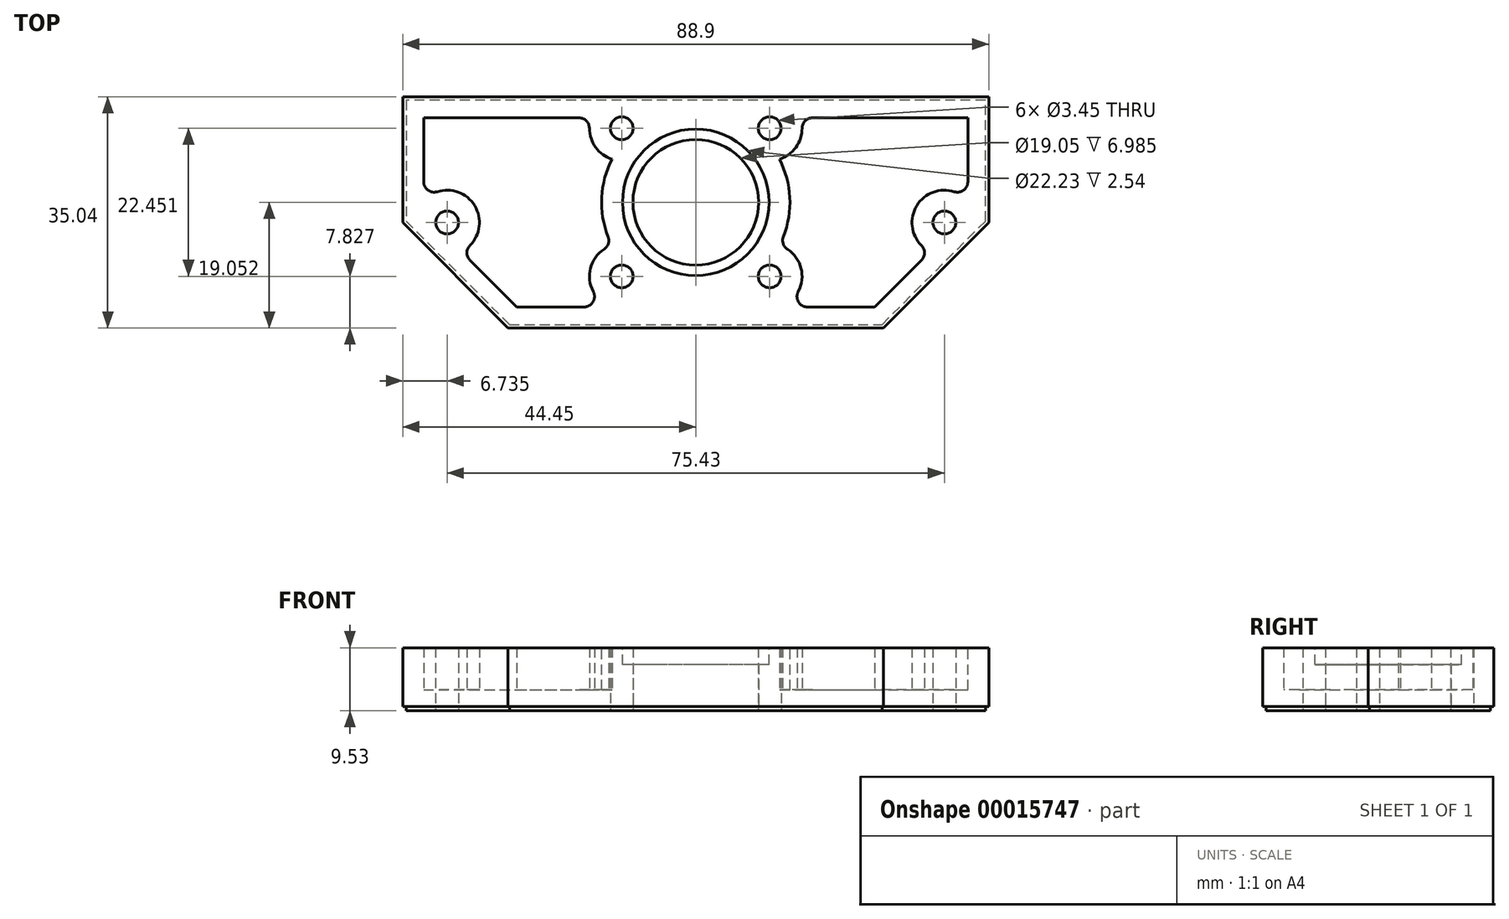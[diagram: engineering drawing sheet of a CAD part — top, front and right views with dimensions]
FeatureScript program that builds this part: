
annotation { "Feature Type Name" : "Feature", "Feature Type Description" : "" }
export const myFeature = defineFeature(function(context is Context, id is Id, definition is map)
    precondition{}
    {
        {
            var Q0;
            Q0=qCreatedBy(makeId("Top.planeOp"),FACE);
            var sketch = newSketch(context, id + "F0", { "sketchPlane" : qUnion([Q0])});
            skLineSegment(sketch, "E0.bottom", {"start": v(0, 0) * mm, "end": v(88.9, 0) * mm});
            skLineSegment(sketch, "E0.left", {"start": v(0, 0) * mm, "end": v(0, -19.05) * mm});
            skLineSegment(sketch, "E0.right", {"start": v(88.9, 0) * mm, "end": v(88.9, -19.05) * mm});
            skLineSegment(sketch, "E1", {"start": v(0, -19.05) * mm, "end": v(15.99, -35.04) * mm});
            skLineSegment(sketch, "E2", {"start": v(88.9, -19.05) * mm, "end": v(72.91, -35.04) * mm});
            skLineSegment(sketch, "E3", {"start": v(15.99, -35.04) * mm, "end": v(72.91, -35.04) * mm});
            skLineSegment(sketch, "E4", {"start": v(0, -19.05) * mm, "end": v(6.74, -19.05) * mm, "construction": true});
            skCircle(sketch, "E5", {"center": v(6.74, -19.05) * mm, "radius": 4.76 * mm, "construction": true});
            skLineSegment(sketch, "E6", {"start": v(88.9, -19.05) * mm, "end": v(82.16, -19.05) * mm, "construction": true});
            skLineSegment(sketch, "E7", {"start": v(44.45, -15.99) * mm, "end": v(44.45, -35.04) * mm, "construction": true});
            skCircle(sketch, "E8", {"center": v(44.45, -15.99) * mm, "radius": 9.53 * mm});
            skCircle(sketch, "E9", {"center": v(6.74, -19.05) * mm, "radius": 1.73 * mm});
            skCircle(sketch, "E10", {"center": v(82.16, -19.05) * mm, "radius": 1.73 * mm});
            skLineSegment(sketch, "E11.bottom", {"start": v(55.68, -27.21) * mm, "end": v(33.22, -27.21) * mm, "construction": true});
            skLineSegment(sketch, "E11.top", {"start": v(55.68, -4.76) * mm, "end": v(33.22, -4.76) * mm, "construction": true});
            skLineSegment(sketch, "E11.left", {"start": v(55.68, -27.21) * mm, "end": v(55.68, -4.76) * mm, "construction": true});
            skLineSegment(sketch, "E11.right", {"start": v(33.22, -27.21) * mm, "end": v(33.22, -4.76) * mm, "construction": true});
            skCircle(sketch, "E12", {"center": v(44.45, -15.99) * mm, "radius": 11.11 * mm, "construction": true});
            skCircle(sketch, "E13", {"center": v(55.68, -4.76) * mm, "radius": 4.76 * mm, "construction": true});
            skCircle(sketch, "E14", {"center": v(33.22, -4.76) * mm, "radius": 1.73 * mm});
            skCircle(sketch, "E15", {"center": v(55.68, -4.76) * mm, "radius": 1.73 * mm});
            skCircle(sketch, "E16", {"center": v(55.68, -27.21) * mm, "radius": 1.73 * mm});
            skCircle(sketch, "E17", {"center": v(33.22, -27.21) * mm, "radius": 1.73 * mm});
            skLineSegment(sketch, "E18", {"start": v(6.74, -19.05) * mm, "end": v(15.99, -19.05) * mm, "construction": true});
            skLineSegment(sketch, "E19", {"start": v(15.99, -19.05) * mm, "end": v(15.99, -35.04) * mm, "construction": true});
            skSolve(sketch);
        }
        {
            var Q0;
            Q0=qSketchRegion(id+"F0",true);
            extrude(context, id + "F1", {"entities" : qUnion([Q0]), "depth" : 9.52 * mm});
        }
        {
            var Q0;
            Q0=makeQuery(id+"F1.opExtrude","CAP_FACE",FACE,{"disambiguationData":[OSD([sQuery(id+"F0.wireOp",EDGE,"E0.bottom"),sQuery(id+"F0.wireOp",EDGE,"E0.left"),sQuery(id+"F0.wireOp",EDGE,"E0.right"),sQuery(id+"F0.wireOp",EDGE,"E1"),sQuery(id+"F0.wireOp",EDGE,"E2"),sQuery(id+"F0.wireOp",EDGE,"E3"),sQuery(id+"F0.wireOp",EDGE,"E8"),sQuery(id+"F0.wireOp",EDGE,"E9"),sQuery(id+"F0.wireOp",EDGE,"E10"),sQuery(id+"F0.wireOp",EDGE,"E14"),sQuery(id+"F0.wireOp",EDGE,"E15"),sQuery(id+"F0.wireOp",EDGE,"E16"),sQuery(id+"F0.wireOp",EDGE,"E17")])],"isStart":false});
            var sketch = newSketch(context, id + "F2", { "sketchPlane" : qUnion([Q0])});
            skCircle(sketch, "E20", {"center": v(44.45, -15.99) * mm, "radius": 11.11 * mm});
            skSolve(sketch);
        }
        {
            var Q0;
            Q0=qSketchRegion(id+"F2",true);
            extrude(context, id + "F3", {"entities" : qUnion([Q0]), "operationType" : NewBodyOperationType.REMOVE, "oppositeDirection" : true, "depth" : 2.54 * mm});
        }
        {
            var Q0;
            Q0=makeQuery(id+"F1.opExtrude","CAP_FACE",FACE,{"disambiguationData":[OSD([sQuery(id+"F0.wireOp",EDGE,"E0.bottom"),sQuery(id+"F0.wireOp",EDGE,"E0.left"),sQuery(id+"F0.wireOp",EDGE,"E0.right"),sQuery(id+"F0.wireOp",EDGE,"E1"),sQuery(id+"F0.wireOp",EDGE,"E2"),sQuery(id+"F0.wireOp",EDGE,"E3"),sQuery(id+"F0.wireOp",EDGE,"E8"),sQuery(id+"F0.wireOp",EDGE,"E9"),sQuery(id+"F0.wireOp",EDGE,"E10"),sQuery(id+"F0.wireOp",EDGE,"E14"),sQuery(id+"F0.wireOp",EDGE,"E15"),sQuery(id+"F0.wireOp",EDGE,"E16"),sQuery(id+"F0.wireOp",EDGE,"E17")])],"isStart":false});
            shell(context, id + "F4", {"entities" : qUnion([Q0]), "thickness" : 3.17 * mm});
        }
        {
            var Q0;
            Q0=makeQuery(id+"F4.opShell","OFFSET_FACE",FACE,{"disambiguationData":[OSD([sQuery(id+"F0.wireOp",EDGE,"E0.bottom"),sQuery(id+"F0.wireOp",EDGE,"E0.left"),sQuery(id+"F0.wireOp",EDGE,"E0.right"),sQuery(id+"F0.wireOp",EDGE,"E1"),sQuery(id+"F0.wireOp",EDGE,"E2"),sQuery(id+"F0.wireOp",EDGE,"E3"),sQuery(id+"F0.wireOp",EDGE,"E8"),sQuery(id+"F0.wireOp",EDGE,"E9"),sQuery(id+"F0.wireOp",EDGE,"E10"),sQuery(id+"F0.wireOp",EDGE,"E14"),sQuery(id+"F0.wireOp",EDGE,"E15"),sQuery(id+"F0.wireOp",EDGE,"E16"),sQuery(id+"F0.wireOp",EDGE,"E17")]),OD(2.0)]});
            var Q1;
            Q1=makeQuery(id+"F4.opShell","OFFSET_FACE",FACE,{"disambiguationData":[OSD([sQuery(id+"F0.wireOp",EDGE,"E0.bottom"),sQuery(id+"F0.wireOp",EDGE,"E0.left"),sQuery(id+"F0.wireOp",EDGE,"E0.right"),sQuery(id+"F0.wireOp",EDGE,"E1"),sQuery(id+"F0.wireOp",EDGE,"E2"),sQuery(id+"F0.wireOp",EDGE,"E3"),sQuery(id+"F0.wireOp",EDGE,"E8"),sQuery(id+"F0.wireOp",EDGE,"E9"),sQuery(id+"F0.wireOp",EDGE,"E10"),sQuery(id+"F0.wireOp",EDGE,"E14"),sQuery(id+"F0.wireOp",EDGE,"E15"),sQuery(id+"F0.wireOp",EDGE,"E16"),sQuery(id+"F0.wireOp",EDGE,"E17")]),OD(3.0)]});
            var Q2;
            Q2=makeQuery(id+"F1.opExtrude","CAP_FACE",FACE,{"disambiguationData":[OSD([sQuery(id+"F0.wireOp",EDGE,"E0.bottom"),sQuery(id+"F0.wireOp",EDGE,"E0.left"),sQuery(id+"F0.wireOp",EDGE,"E0.right"),sQuery(id+"F0.wireOp",EDGE,"E1"),sQuery(id+"F0.wireOp",EDGE,"E2"),sQuery(id+"F0.wireOp",EDGE,"E3"),sQuery(id+"F0.wireOp",EDGE,"E8"),sQuery(id+"F0.wireOp",EDGE,"E9"),sQuery(id+"F0.wireOp",EDGE,"E10"),sQuery(id+"F0.wireOp",EDGE,"E14"),sQuery(id+"F0.wireOp",EDGE,"E15"),sQuery(id+"F0.wireOp",EDGE,"E16"),sQuery(id+"F0.wireOp",EDGE,"E17")])],"isStart":false});
            extrude(context, id + "F5", {"entities" : qUnion([Q0, Q1]), "operationType" : NewBodyOperationType.ADD, "endBound" : BoundingType.UP_TO_SURFACE, "endBoundEntityFace" : qUnion([Q2]), "depth" : 25.4 * mm});
        }
        {
            var Q0;
            Q0=makeQuery(id+"F4.opShell","TWEAK_EDGE",EDGE,{"derivedFrom":[makeQuery(id+"F1.opExtrude","SWEPT_FACE",FACE,{"disambiguationData":[OSD([sQuery(id+"F0.wireOp",EDGE,"E0.left")])]}),makeQuery(id+"F1.opExtrude","SWEPT_FACE",FACE,{"disambiguationData":[OSD([sQuery(id+"F0.wireOp",EDGE,"E9")])]})]});
            var Q1;
            Q1=makeQuery(id+"F4.opShell","TWEAK_EDGE",EDGE,{"derivedFrom":[makeQuery(id+"F1.opExtrude","SWEPT_FACE",FACE,{"disambiguationData":[OSD([sQuery(id+"F0.wireOp",EDGE,"E1")])]}),makeQuery(id+"F1.opExtrude","SWEPT_FACE",FACE,{"disambiguationData":[OSD([sQuery(id+"F0.wireOp",EDGE,"E9")])]})]});
            var Q2;
            Q2=makeQuery(id+"F4.opShell","TWEAK_EDGE",EDGE,{"disambiguationData":[OD(0.0)],"derivedFrom":[makeQuery(id+"F1.opExtrude","SWEPT_FACE",FACE,{"disambiguationData":[OSD([sQuery(id+"F0.wireOp",EDGE,"E3")])]}),makeQuery(id+"F1.opExtrude","SWEPT_FACE",FACE,{"disambiguationData":[OSD([sQuery(id+"F0.wireOp",EDGE,"E17")])]})]});
            var Q3;
            Q3=makeQuery(id+"F4.opShell","TWEAK_EDGE",EDGE,{"disambiguationData":[OD(0.0)],"derivedFrom":[makeQuery(id+"F1.opExtrude","SWEPT_FACE",FACE,{"disambiguationData":[OSD([sQuery(id+"F0.wireOp",EDGE,"E0.bottom")])]}),makeQuery(id+"F1.opExtrude","SWEPT_FACE",FACE,{"disambiguationData":[OSD([sQuery(id+"F0.wireOp",EDGE,"E14")])]})]});
            var Q4;
            Q4=makeQuery(id+"F4.opShell","TWEAK_EDGE",EDGE,{"disambiguationData":[OD(0.0)],"derivedFrom":[makeQuery(id+"F1.opExtrude","SWEPT_FACE",FACE,{"disambiguationData":[OSD([sQuery(id+"F0.wireOp",EDGE,"E0.bottom")])]}),makeQuery(id+"F1.opExtrude","SWEPT_FACE",FACE,{"disambiguationData":[OSD([sQuery(id+"F0.wireOp",EDGE,"E15")])]})]});
            var Q5;
            Q5=makeQuery(id+"F4.opShell","TWEAK_EDGE",EDGE,{"disambiguationData":[OD(0.0)],"derivedFrom":[makeQuery(id+"F1.opExtrude","SWEPT_FACE",FACE,{"disambiguationData":[OSD([sQuery(id+"F0.wireOp",EDGE,"E3")])]}),makeQuery(id+"F1.opExtrude","SWEPT_FACE",FACE,{"disambiguationData":[OSD([sQuery(id+"F0.wireOp",EDGE,"E16")])]})]});
            var Q6;
            Q6=makeQuery(id+"F4.opShell","TWEAK_EDGE",EDGE,{"derivedFrom":[makeQuery(id+"F1.opExtrude","SWEPT_FACE",FACE,{"disambiguationData":[OSD([sQuery(id+"F0.wireOp",EDGE,"E2")])]}),makeQuery(id+"F1.opExtrude","SWEPT_FACE",FACE,{"disambiguationData":[OSD([sQuery(id+"F0.wireOp",EDGE,"E10")])]})]});
            var Q7;
            Q7=makeQuery(id+"F4.opShell","TWEAK_EDGE",EDGE,{"derivedFrom":[makeQuery(id+"F1.opExtrude","SWEPT_FACE",FACE,{"disambiguationData":[OSD([sQuery(id+"F0.wireOp",EDGE,"E0.right")])]}),makeQuery(id+"F1.opExtrude","SWEPT_FACE",FACE,{"disambiguationData":[OSD([sQuery(id+"F0.wireOp",EDGE,"E10")])]})]});
            var Q8;
            Q8=makeQuery(id+"F4.opShell","TWEAK_EDGE",EDGE,{"disambiguationData":[OD(0.0)],"derivedFrom":[makeQuery(id+"F1.opExtrude","SWEPT_FACE",FACE,{"disambiguationData":[OSD([sQuery(id+"F0.wireOp",EDGE,"E17")])]}),makeQuery(id+"F3.boolean.opBoolean","COPY",FACE,{"derivedFrom":makeQuery(id+"F3.opExtrude","SWEPT_FACE",FACE,{"disambiguationData":[OSD([sQuery(id+"F2.wireOp",EDGE,"E20")])]})})]});
            var Q9;
            Q9=makeQuery(id+"F4.opShell","TWEAK_EDGE",EDGE,{"disambiguationData":[OD(0.0)],"derivedFrom":[makeQuery(id+"F1.opExtrude","SWEPT_FACE",FACE,{"disambiguationData":[OSD([sQuery(id+"F0.wireOp",EDGE,"E16")])]}),makeQuery(id+"F3.boolean.opBoolean","COPY",FACE,{"derivedFrom":makeQuery(id+"F3.opExtrude","SWEPT_FACE",FACE,{"disambiguationData":[OSD([sQuery(id+"F2.wireOp",EDGE,"E20")])]})})]});
            fillet(context, id + "F6", {"entities" : qUnion([Q0, Q1, Q2, Q3, Q4, Q5, Q6, Q7, Q8, Q9]), "radius" : 1.59 * mm, "tangentPropagation" : true, "allowEdgeOverflow" : false});
        }
        {
            var Q0;
            {var subQ0=sQuery(id+"F2.wireOp",EDGE,"E20");Q0=makeQuery(id+"F4.opShell","OFFSET_FACE",FACE,{"disambiguationData":[OSD([subQ0]),TDD([makeQuery(id+"F3.boolean.opBoolean","COPY",FACE,{"derivedFrom":makeQuery(id+"F3.opExtrude","CAP_FACE",FACE,{"disambiguationData":[OSD([subQ0])],"isStart":false})})]),OD(1.0)]});}
            var Q1;
            {var subQ0=sQuery(id+"F2.wireOp",EDGE,"E20");Q1=makeQuery(id+"F4.opShell","OFFSET_FACE",FACE,{"disambiguationData":[OSD([subQ0]),TDD([makeQuery(id+"F3.boolean.opBoolean","COPY",FACE,{"derivedFrom":makeQuery(id+"F3.opExtrude","CAP_FACE",FACE,{"disambiguationData":[OSD([subQ0])],"isStart":false})})]),OD(2.0)]});}
            var Q2;
            Q2=makeQuery(id+"F1.opExtrude","CAP_FACE",FACE,{"disambiguationData":[OSD([sQuery(id+"F0.wireOp",EDGE,"E0.bottom"),sQuery(id+"F0.wireOp",EDGE,"E0.left"),sQuery(id+"F0.wireOp",EDGE,"E0.right"),sQuery(id+"F0.wireOp",EDGE,"E1"),sQuery(id+"F0.wireOp",EDGE,"E2"),sQuery(id+"F0.wireOp",EDGE,"E3"),sQuery(id+"F0.wireOp",EDGE,"E8"),sQuery(id+"F0.wireOp",EDGE,"E9"),sQuery(id+"F0.wireOp",EDGE,"E10"),sQuery(id+"F0.wireOp",EDGE,"E14"),sQuery(id+"F0.wireOp",EDGE,"E15"),sQuery(id+"F0.wireOp",EDGE,"E16"),sQuery(id+"F0.wireOp",EDGE,"E17")])],"isStart":true});
            extrude(context, id + "F7", {"entities" : qUnion([Q0, Q1]), "operationType" : NewBodyOperationType.ADD, "endBound" : BoundingType.UP_TO_SURFACE, "endBoundEntityFace" : qUnion([Q2]), "depth" : 25.4 * mm});
        }
        {
            var Q0;
            Q0=makeQuery(id+"F1.opExtrude","SWEPT_FACE",FACE,{"disambiguationData":[OSD([sQuery(id+"F0.wireOp",EDGE,"E0.right")])]});
            var sketch = newSketch(context, id + "F8", { "sketchPlane" : qUnion([Q0])});
            skLineSegment(sketch, "E21.bottom", {"start": v(0, 0) * mm, "end": v(-0.5, 0) * mm});
            skLineSegment(sketch, "E21.top", {"start": v(0, 0.64) * mm, "end": v(-0.5, 0.64) * mm});
            skLineSegment(sketch, "E21.left", {"start": v(0, 0) * mm, "end": v(0, 0.64) * mm});
            skLineSegment(sketch, "E21.right", {"start": v(-0.5, 0) * mm, "end": v(-0.5, 0.64) * mm});
            skSolve(sketch);
        }
        {
            var Q0;
            Q0=makeQuery(id+"F8.imprint","IMPRINT",FACE,{"disambiguationData":[TD([[makeQuery(id+"F8.imprint","IMPRINT",EDGE,{"derivedFrom":sQuery(id+"F8.wireOp",EDGE,"E21.bottom")}),-1.0]])]});
            var Q1;
            Q1=makeQuery(id+"F1.opExtrude","CAP_EDGE",EDGE,{"disambiguationData":[OSD([sQuery(id+"F0.wireOp",EDGE,"E0.bottom")])],"isStart":true});
            var Q2;
            Q2=makeQuery(id+"F1.opExtrude","CAP_EDGE",EDGE,{"disambiguationData":[OSD([sQuery(id+"F0.wireOp",EDGE,"E0.left")])],"isStart":true});
            var Q3;
            Q3=makeQuery(id+"F1.opExtrude","CAP_EDGE",EDGE,{"disambiguationData":[OSD([sQuery(id+"F0.wireOp",EDGE,"E1")])],"isStart":true});
            var Q4;
            Q4=makeQuery(id+"F1.opExtrude","CAP_EDGE",EDGE,{"disambiguationData":[OSD([sQuery(id+"F0.wireOp",EDGE,"E3")])],"isStart":true});
            var Q5;
            Q5=makeQuery(id+"F1.opExtrude","CAP_EDGE",EDGE,{"disambiguationData":[OSD([sQuery(id+"F0.wireOp",EDGE,"E2")])],"isStart":true});
            var Q6;
            Q6=makeQuery(id+"F1.opExtrude","CAP_EDGE",EDGE,{"disambiguationData":[OSD([sQuery(id+"F0.wireOp",EDGE,"E0.right")])],"isStart":true});
            sweep(context, id + "F9", {"operationType" : NewBodyOperationType.REMOVE, "profiles" : qUnion([Q0]), "path" : qUnion([Q1, Q2, Q3, Q4, Q5, Q6])});
        }
    });
